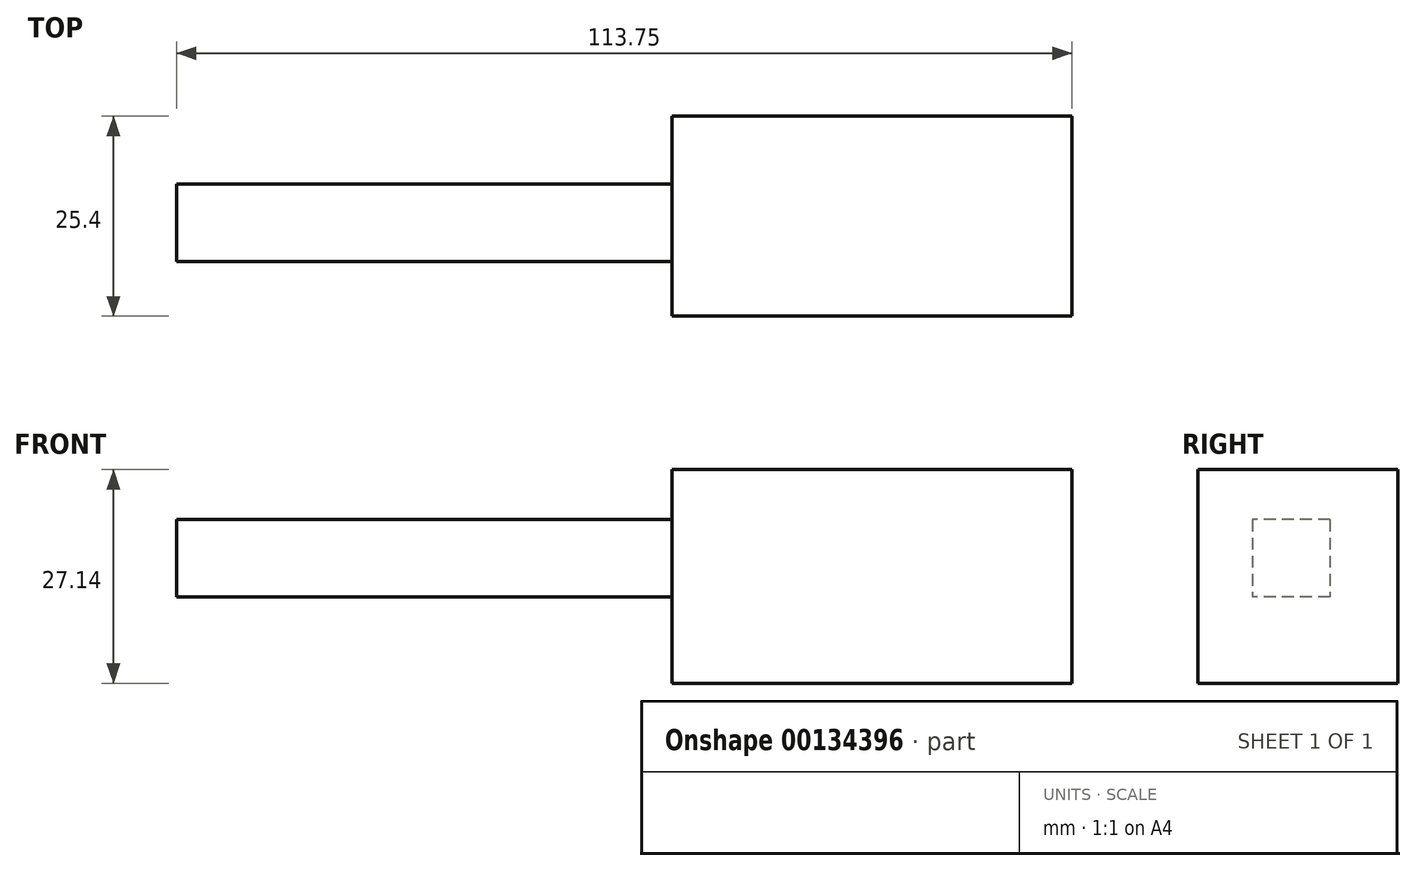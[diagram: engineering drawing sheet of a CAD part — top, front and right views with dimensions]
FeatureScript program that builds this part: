
annotation { "Feature Type Name" : "Feature", "Feature Type Description" : "" }
export const myFeature = defineFeature(function(context is Context, id is Id, definition is map)
    precondition{}
    {
        {
            var Q0;
            Q0=qCreatedBy(makeId("Front.planeOp"),FACE);
            var sketch = newSketch(context, id + "F0", { "sketchPlane" : qUnion([Q0])});
            skLineSegment(sketch, "E0.bottom", {"start": v(-70.52, 32.99) * mm, "end": v(-19.72, 32.99) * mm});
            skLineSegment(sketch, "E0.top", {"start": v(-70.52, 5.85) * mm, "end": v(-19.72, 5.85) * mm});
            skLineSegment(sketch, "E0.left", {"start": v(-70.52, 32.99) * mm, "end": v(-70.52, 5.85) * mm});
            skLineSegment(sketch, "E0.right", {"start": v(-19.72, 32.99) * mm, "end": v(-19.72, 5.85) * mm});
            skSolve(sketch);
        }
        {
            var Q0;
            Q0=makeQuery(id+"F0.imprint","IMPRINT",FACE,{"disambiguationData":[TD([[makeQuery(id+"F0.imprint","IMPRINT",EDGE,{"derivedFrom":sQuery(id+"F0.wireOp",EDGE,"E0.bottom")}),-1.0]])]});
            extrude(context, id + "F1", {"entities" : qUnion([Q0]), "depth" : 25.4 * mm});
        }
        {
            var Q0;
            Q0=makeQuery(id+"F1.opExtrude","SWEPT_FACE",FACE,{"disambiguationData":[OSD([sQuery(id+"F0.wireOp",EDGE,"E0.left")])]});
            extrude(context, id + "F2", {"entities" : qUnion([Q0]), "operationType" : NewBodyOperationType.ADD, "oppositeDirection" : true, "depth" : 25.4 * mm});
        }
        {
            var Q0;
            Q0=makeQuery(id+"F1.opExtrude","SWEPT_FACE",FACE,{"disambiguationData":[OSD([sQuery(id+"F0.wireOp",EDGE,"E0.left")])]});
            var sketch = newSketch(context, id + "F3", { "sketchPlane" : qUnion([Q0])});
            skSolve(sketch);
        }
        {
            var Q0;
            {var subQ0=sQuery(id+"F0.wireOp",EDGE,"E0.left");Q0=makeQuery(id+"F3.imprint","IMPRINT",FACE,{"disambiguationData":[TD([[makeQuery(id+"F3.imprint","IMPRINT",EDGE,{"derivedFrom":makeQuery(id+"F1.opExtrude","CAP_EDGE",EDGE,{"disambiguationData":[OSD([subQ0])],"isStart":true})}),1.0]])]});}
            var sketch = newSketch(context, id + "F4", { "sketchPlane" : qUnion([Q0])});
            skLineSegment(sketch, "E1.bottom", {"start": v(8.61, 26.64) * mm, "end": v(18.46, 26.64) * mm});
            skLineSegment(sketch, "E1.top", {"start": v(8.61, 16.85) * mm, "end": v(18.46, 16.85) * mm});
            skLineSegment(sketch, "E1.left", {"start": v(8.61, 26.64) * mm, "end": v(8.61, 16.85) * mm});
            skLineSegment(sketch, "E1.right", {"start": v(18.46, 26.64) * mm, "end": v(18.46, 16.85) * mm});
            skSolve(sketch);
        }
        {
            var Q0;
            Q0=makeQuery(id+"F4.imprint","IMPRINT",FACE,{"disambiguationData":[TD([[makeQuery(id+"F4.imprint","IMPRINT",EDGE,{"derivedFrom":sQuery(id+"F4.wireOp",EDGE,"E1.bottom")}),-1.0]])]});
            extrude(context, id + "F5", {"entities" : qUnion([Q0]), "operationType" : NewBodyOperationType.ADD, "endBound" : BoundingType.THROUGH_ALL, "depth" : 25.4 * mm});
        }
    });
